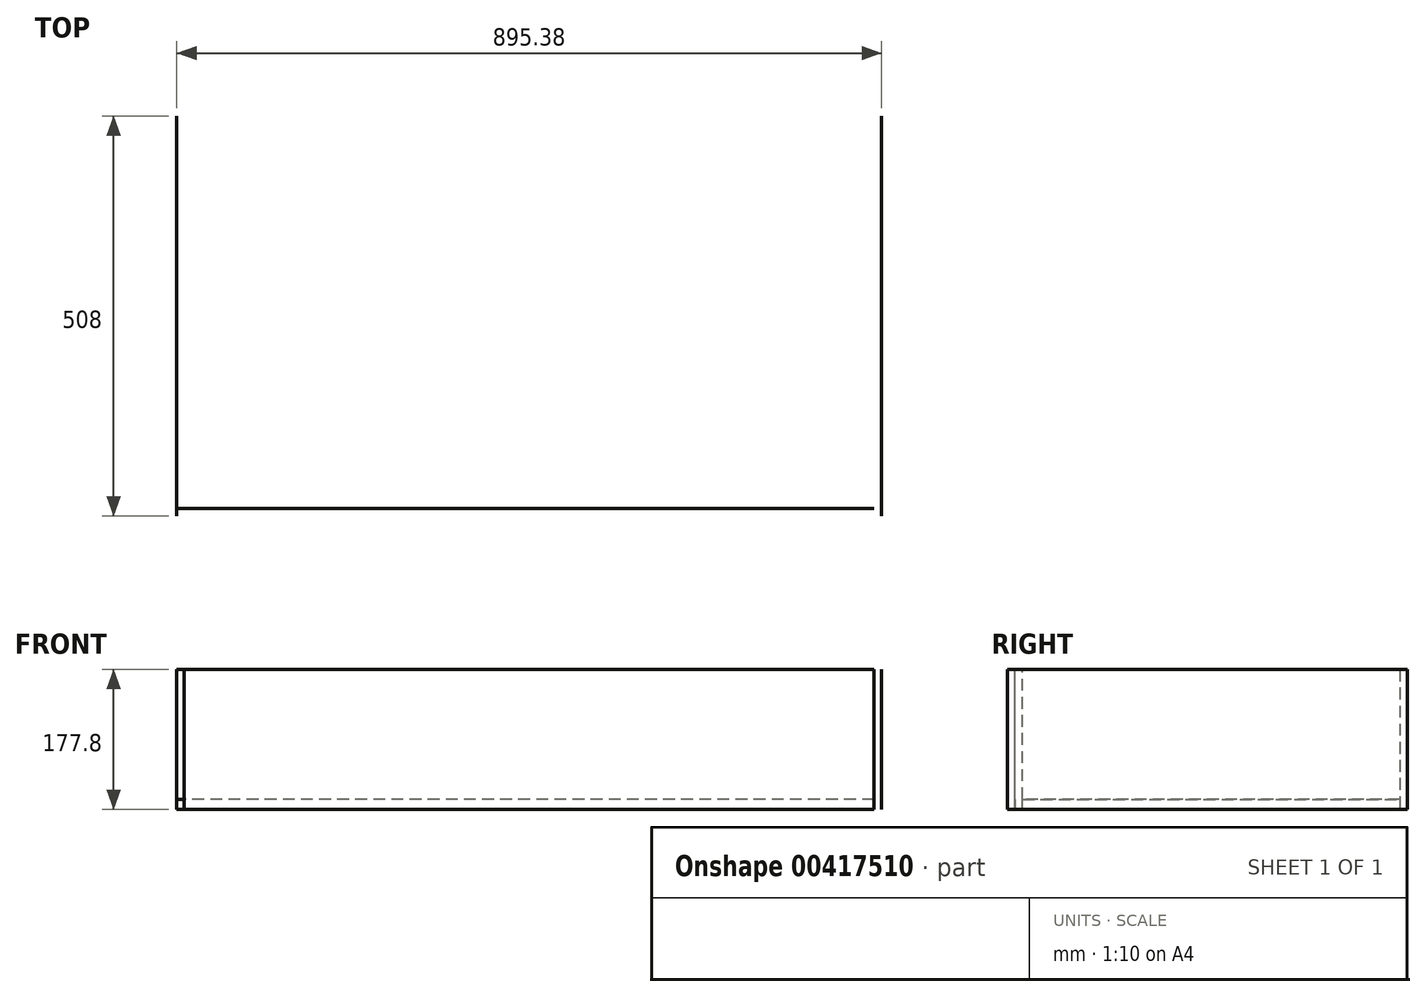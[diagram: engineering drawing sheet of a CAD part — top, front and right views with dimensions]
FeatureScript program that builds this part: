
annotation { "Feature Type Name" : "Feature", "Feature Type Description" : "" }
export const myFeature = defineFeature(function(context is Context, id is Id, definition is map)
    precondition{}
    {
        {
            assignVariable(context, id + "F0", {"name" : "SideThickness", "anyValue" : 3 / 101.6 * mm});
        }
        {
            assignVariable(context, id + "F1", {"name" : "BottomThickness", "anyValue" : 0.25});
        }
        {
            var Q0;
            Q0=qCreatedBy(makeId("Top.planeOp"),FACE);
            var sketch = newSketch(context, id + "F2", { "sketchPlane" : qUnion([Q0])});
            skLineSegment(sketch, "E0.bottom", {"start": v(447.68, -244.47) * mm, "end": v(-447.68, -244.47) * mm});
            skLineSegment(sketch, "E0.top", {"start": v(447.68, 244.47) * mm, "end": v(-447.68, 244.47) * mm});
            skLineSegment(sketch, "E0.left", {"start": v(447.68, -244.47) * mm, "end": v(447.68, 244.47) * mm});
            skLineSegment(sketch, "E0.right", {"start": v(-447.68, -244.47) * mm, "end": v(-447.68, 244.47) * mm});
            skPoint(sketch, "E0.middle", {"position": v(0, 0) * mm});
            skSolve(sketch);
        }
        {
            var Q0;
            Q0 = qSketchRegion(id + "F2", true);
            extrude(context, id + "F3", {"entities" : qUnion([Q0]), "depth" : (getVariable(context, 'BottomThickness')) * mm});
        }
        {
            var Q0;
            Q0=makeQuery(id+"F3.opExtrude","SWEPT_FACE",FACE,{"disambiguationData":[OSD([sQuery(id+"F2.wireOp",EDGE,"E0.left")])]});
            var sketch = newSketch(context, id + "F4", { "sketchPlane" : qUnion([Q0])});
            skLineSegment(sketch, "E1.bottom", {"start": v(-254, -12.7) * mm, "end": v(254, -12.7) * mm});
            skLineSegment(sketch, "E1.top", {"start": v(-254, 165.1) * mm, "end": v(254, 165.1) * mm});
            skLineSegment(sketch, "E1.left", {"start": v(-254, -12.7) * mm, "end": v(-254, 165.1) * mm});
            skLineSegment(sketch, "E1.right", {"start": v(254, -12.7) * mm, "end": v(254, 165.1) * mm});
            skSolve(sketch);
        }
        {
            var Q0;
            Q0 = qSketchRegion(id + "F4", true);
            extrude(context, id + "F5", {"entities" : qUnion([Q0]), "endBound" : BoundingType.SYMMETRIC, "depth" : getVariable(context, 'SideThickness')});
        }
        {
            var Q0;
            Q0=makeQuery(id+"F3.opExtrude","SWEPT_FACE",FACE,{"disambiguationData":[OSD([sQuery(id+"F2.wireOp",EDGE,"E0.bottom")])]});
            var sketch = newSketch(context, id + "F6", { "sketchPlane" : qUnion([Q0])});
            skLineSegment(sketch, "E2.bottom", {"start": v(-447.68, -12.7) * mm, "end": v(447.67, -12.7) * mm});
            skLineSegment(sketch, "E2.top", {"start": v(-447.68, 165.1) * mm, "end": v(447.68, 165.1) * mm});
            skLineSegment(sketch, "E2.left", {"start": v(-447.68, -12.7) * mm, "end": v(-447.68, 165.1) * mm});
            skLineSegment(sketch, "E2.right", {"start": v(447.68, -12.7) * mm, "end": v(447.68, 165.1) * mm});
            skSolve(sketch);
        }
        {
            var Q0;
            Q0 = qSketchRegion(id + "F6", true);
            extrude(context, id + "F7", {"entities" : qUnion([Q0]), "endBound" : BoundingType.SYMMETRIC, "oppositeDirection" : true, "depth" : getVariable(context, 'SideThickness')});
        }
        {
            var Q0;
            Q0=makeQuery(id+"F7.opExtrude","SWEPT_FACE",FACE,{"disambiguationData":[OSD([sQuery(id+"F6.wireOp",EDGE,"E2.top")])]});
            var sketch = newSketch(context, id + "F8", { "sketchPlane" : qUnion([Q0])});
            skLineSegment(sketch, "E3.bottom", {"start": v(-447.68, -254) * mm, "end": v(-438.15, -254) * mm});
            skLineSegment(sketch, "E3.top", {"start": v(-447.68, -244.47) * mm, "end": v(-438.15, -244.47) * mm});
            skLineSegment(sketch, "E3.left", {"start": v(-447.68, -254) * mm, "end": v(-447.68, -244.47) * mm});
            skLineSegment(sketch, "E3.right", {"start": v(-438.15, -254) * mm, "end": v(-438.15, -244.47) * mm});
            skLineSegment(sketch, "E4.MirrorCS", {"start": v(447.68, -254) * mm, "end": v(447.68, -244.47) * mm});
            skLineSegment(sketch, "E5.MirrorCS", {"start": v(438.15, -254) * mm, "end": v(438.15, -244.47) * mm});
            skLineSegment(sketch, "E6.MirrorCS", {"start": v(447.68, -244.47) * mm, "end": v(438.15, -244.47) * mm});
            skLineSegment(sketch, "E7.MirrorCS", {"start": v(447.68, -254) * mm, "end": v(438.15, -254) * mm});
            skSolve(sketch);
        }
        {
            var Q0;
            Q0 = qSketchRegion(id + "F8", true);
            var Q1;
            Q1=makeQuery(id+"F7.opExtrude","SWEPT_FACE",FACE,{"disambiguationData":[OSD([sQuery(id+"F6.wireOp",EDGE,"E2.bottom")])]});
            extrude(context, id + "F9", {"entities" : qUnion([Q0]), "operationType" : NewBodyOperationType.REMOVE, "endBound" : BoundingType.UP_TO_SURFACE, "oppositeDirection" : true, "endBoundEntityFace" : qUnion([Q1]), "depth" : 25.4 * mm});
        }
        {
            var Q0;
            Q0=makeQuery(id+"F5.opExtrude","SWEPT_FACE",FACE,{"disambiguationData":[OSD([sQuery(id+"F4.wireOp",EDGE,"E1.top")])]});
            var sketch = newSketch(context, id + "F10", { "sketchPlane" : qUnion([Q0])});
            skPoint(sketch, "E8.0", {"position": v(447.68, -234.95) * mm});
            skPoint(sketch, "E8.1", {"position": v(438.15, -244.47) * mm});
            skLineSegment(sketch, "E9.bottom", {"start": v(447.68, -234.95) * mm, "end": v(438.15, -234.95) * mm});
            skLineSegment(sketch, "E9.top", {"start": v(447.68, -244.47) * mm, "end": v(438.15, -244.47) * mm});
            skLineSegment(sketch, "E9.left", {"start": v(447.68, -234.95) * mm, "end": v(447.68, -244.47) * mm});
            skLineSegment(sketch, "E9.right", {"start": v(438.15, -234.95) * mm, "end": v(438.15, -244.47) * mm});
            skSolve(sketch);
        }
        {
            var Q0;
            Q0 = qSketchRegion(id + "F10", true);
            var Q1;
            Q1=makeQuery(id+"F5.opExtrude","SWEPT_FACE",FACE,{"disambiguationData":[OSD([sQuery(id+"F4.wireOp",EDGE,"E1.bottom")])]});
            extrude(context, id + "F11", {"entities" : qUnion([Q0]), "operationType" : NewBodyOperationType.REMOVE, "endBound" : BoundingType.UP_TO_SURFACE, "oppositeDirection" : true, "endBoundEntityFace" : qUnion([Q1]), "depth" : 25.4 * mm});
        }
        {
            var Q0;
            Q0=makeQuery(id+"F5.opExtrude","SWEPT_BODY",BODY,{"disambiguationData":[OSD([sQuery(id+"F4.wireOp",EDGE,"E1.bottom"),sQuery(id+"F4.wireOp",EDGE,"E1.top"),sQuery(id+"F4.wireOp",EDGE,"E1.left"),sQuery(id+"F4.wireOp",EDGE,"E1.right")])]});
            var Q1;
            Q1=qCreatedBy(makeId("Right.planeOp"),FACE);
            mirror(context, id + "F12", {"entities" : qUnion([Q0]), "mirrorPlane" : qUnion([Q1])});
        }
        {
            var Q0;
            Q0=makeQuery(id+"F7.opExtrude","SWEPT_BODY",BODY,{"disambiguationData":[OSD([sQuery(id+"F6.wireOp",EDGE,"E2.bottom"),sQuery(id+"F6.wireOp",EDGE,"E2.top"),sQuery(id+"F6.wireOp",EDGE,"E2.left"),sQuery(id+"F6.wireOp",EDGE,"E2.right")])]});
            var Q1;
            Q1=qCreatedBy(makeId("Front.planeOp"),FACE);
            mirror(context, id + "F13", {"entities" : qUnion([Q0]), "mirrorPlane" : qUnion([Q1])});
        }
        {
            var Q0;
            Q0=makeQuery(id+"F3.opExtrude","CAP_FACE",FACE,{"disambiguationData":[OSD([sQuery(id+"F2.wireOp",EDGE,"E0.bottom"),sQuery(id+"F2.wireOp",EDGE,"E0.top"),sQuery(id+"F2.wireOp",EDGE,"E0.left"),sQuery(id+"F2.wireOp",EDGE,"E0.right")])],"isStart":false});
            extrude(context, id + "F14", {"entities" : qUnion([Q0]), "operationType" : NewBodyOperationType.REMOVE, "endBound" : BoundingType.UP_TO_NEXT, "oppositeDirection" : true, "depth" : 25.4 * mm});
        }
        {
            var Q0;
            Q0=makeQuery(id+"F13.opPattern","COPY",FACE,{"derivedFrom":makeQuery(id+"F7.opExtrude","SWEPT_FACE",FACE,{"disambiguationData":[OSD([sQuery(id+"F6.wireOp",EDGE,"E2.bottom")])]}),"instanceName":"1"});
            var Q1;
            Q1=makeQuery(id+"F13.opPattern","COPY",FACE,{"derivedFrom":makeQuery(id+"F7.opExtrude","SWEPT_FACE",FACE,{"disambiguationData":[OSD([sQuery(id+"F6.wireOp",EDGE,"E2.top")])]}),"instanceName":"1"});
            extrude(context, id + "F15", {"entities" : qUnion([Q0]), "operationType" : NewBodyOperationType.REMOVE, "endBound" : BoundingType.UP_TO_SURFACE, "oppositeDirection" : true, "endBoundEntityFace" : qUnion([Q1]), "depth" : 25.4 * mm});
        }
    });
